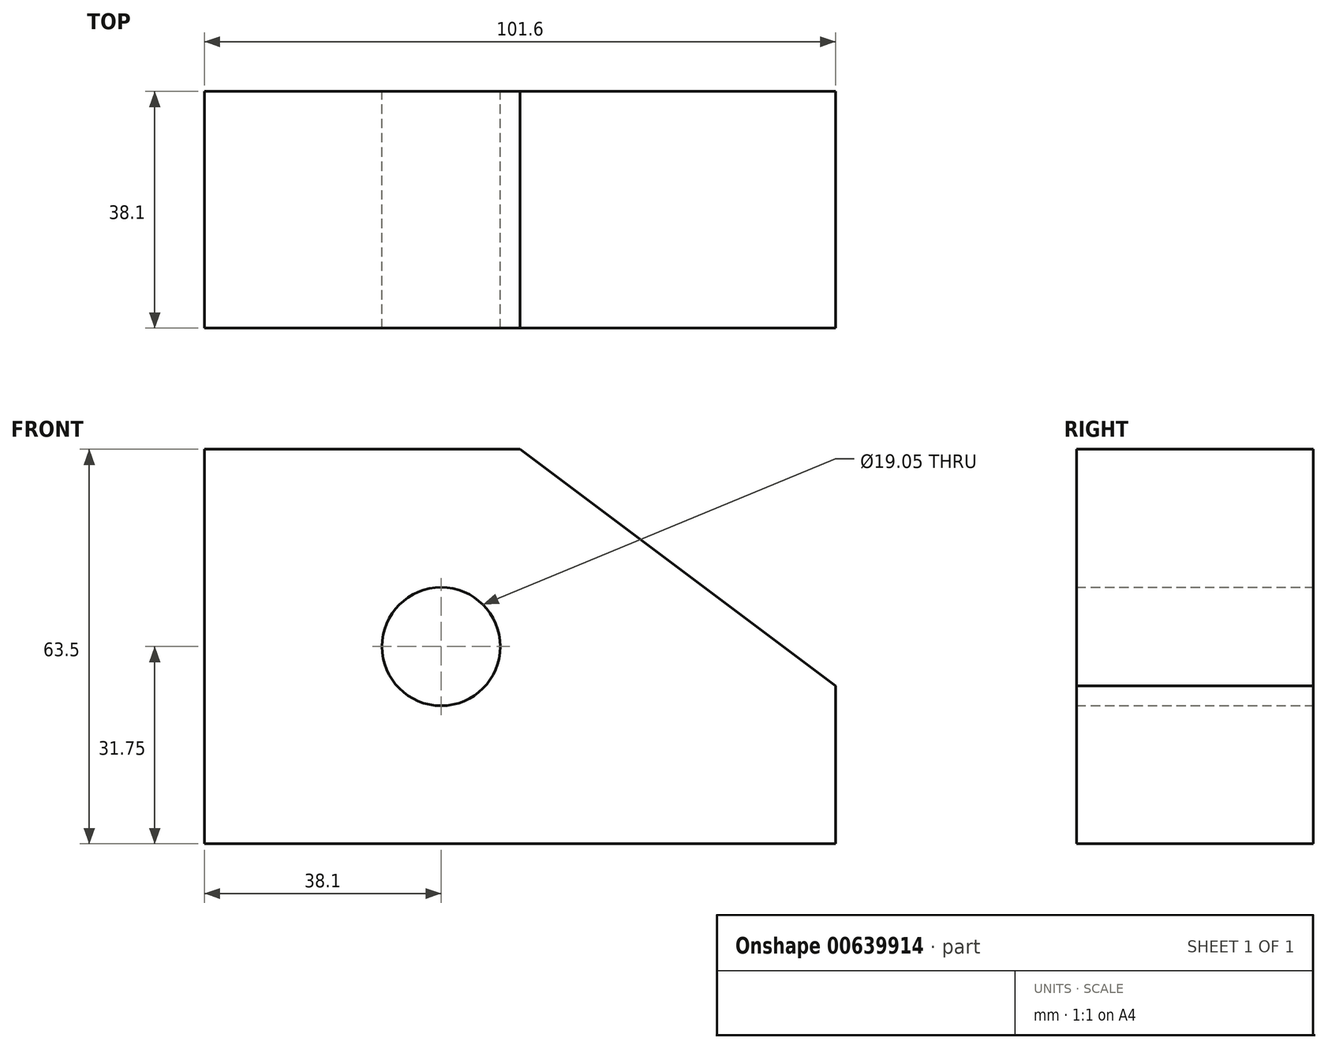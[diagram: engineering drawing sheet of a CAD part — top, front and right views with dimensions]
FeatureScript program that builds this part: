
annotation { "Feature Type Name" : "Feature", "Feature Type Description" : "" }
export const myFeature = defineFeature(function(context is Context, id is Id, definition is map)
    precondition{}
    {
        {
            var Q0;
            Q0=qCreatedBy(makeId("Front.planeOp"),FACE);
            var sketch = newSketch(context, id + "F0", { "sketchPlane" : qUnion([Q0])});
            skLineSegment(sketch, "E0", {"start": v(0, 0) * mm, "end": v(-101.6, 0) * mm});
            skLineSegment(sketch, "E1", {"start": v(0, 0) * mm, "end": v(0, 25.4) * mm});
            skLineSegment(sketch, "E2", {"start": v(-101.6, 0) * mm, "end": v(-101.6, 63.5) * mm});
            skLineSegment(sketch, "E3", {"start": v(-101.6, 63.5) * mm, "end": v(-50.8, 63.5) * mm});
            skLineSegment(sketch, "E4", {"start": v(-50.8, 63.5) * mm, "end": v(0, 25.4) * mm});
            skCircle(sketch, "E5", {"center": v(-63.5, 31.75) * mm, "radius": 9.53 * mm});
            skSolve(sketch);
        }
        {
            var Q0;
            Q0=makeQuery(id+"F0.imprint","IMPRINT",FACE,{"disambiguationData":[TD([[makeQuery(id+"F0.imprint","IMPRINT",EDGE,{"derivedFrom":sQuery(id+"F0.wireOp",EDGE,"E0")}),-1.0]])]});
            extrude(context, id + "F1", {"entities" : qUnion([Q0]), "depth" : 38.1 * mm, "offsetDistance" : 25.4 * mm});
        }
    });
